# Revit family: NBS_CordekLtd_DprssrztnSmps_RadonSump
name_source: partatom
category: Specialty Equipment
revit_build: Autodesk Revit 2014 (Build: 20131024_2115(x64)
units: mm (PartAtom-declared; Revit-internal decimal feet)

## types (1)
- RadonSump
    AssetType = Fixed
    BIMObjectName = NBS_CordekLtd_DepressurizationSumps_RadonSump
    Category = Pr_65_52_25_23:Depressurization sumps
    Color = Black
    Description = Polypropylene radon sump
    DurationUnit = year
    Features = Can reduce the risk posed by radon gas by minimizing the pressure beneath the building
    Height = 240 mm  [stored 0.787402 ft]
    IfcExportAs = IfcDistributionChamberElementType
    IfcExportType = SUMP
    InletsOutletsAngleOfInletOutlet = 90°
    InletsOutletsDiameter = 110 mm
    InletsOutletsNumberOfInletsOutlets = Five
    Length = 510 mm  [stored 1.67323 ft]
    ManufacturerName = Cordek Ltd
    ManufacturerURL = www.cordek.com
    Material = Polypropylene
    ModelReference = Radon Sump
    NBSCertification = http://www.nationalbimlibrary.com
    NBSDescription = Depressurization sumps
    NBSReference = 90-05-20/448
    Name = DepressurizationSumps_RadonSump_CordekLtd
    NominalHeight = 240 mm  [stored 0.787402 ft]
    NominalLength = 510 mm  [stored 1.67323 ft]
    NominalWidth = 510 mm  [stored 1.67323 ft]
    ProductInformation = www.cordek.com/uploads/data_sheets/M-DS15_radon_sump_data_sheet_v2_cordek.pdf
    RadonSumpMaterial = NBS_Concept
    ServiceableArea = >250 m²
    Shape = Circular
    Size = 510 x 510 x 240 mm
    Uniclass2015Description = Depressurization sumps
    Uniclass2015Reference = Pr_65_52_25_23
    Uniclass2015Version = Products v1.1
    Version = 1
    WarrantyDurationUnit = year
    Width = 510 mm  [stored 1.67323 ft]

note: [stored X ft] marks values corroborated as IEEE doubles in the binary element streams (Revit-internal decimal feet)

## geometry (parser evidence)
native form markers: Sweep x1
no freeform markers — native parametric forms only
